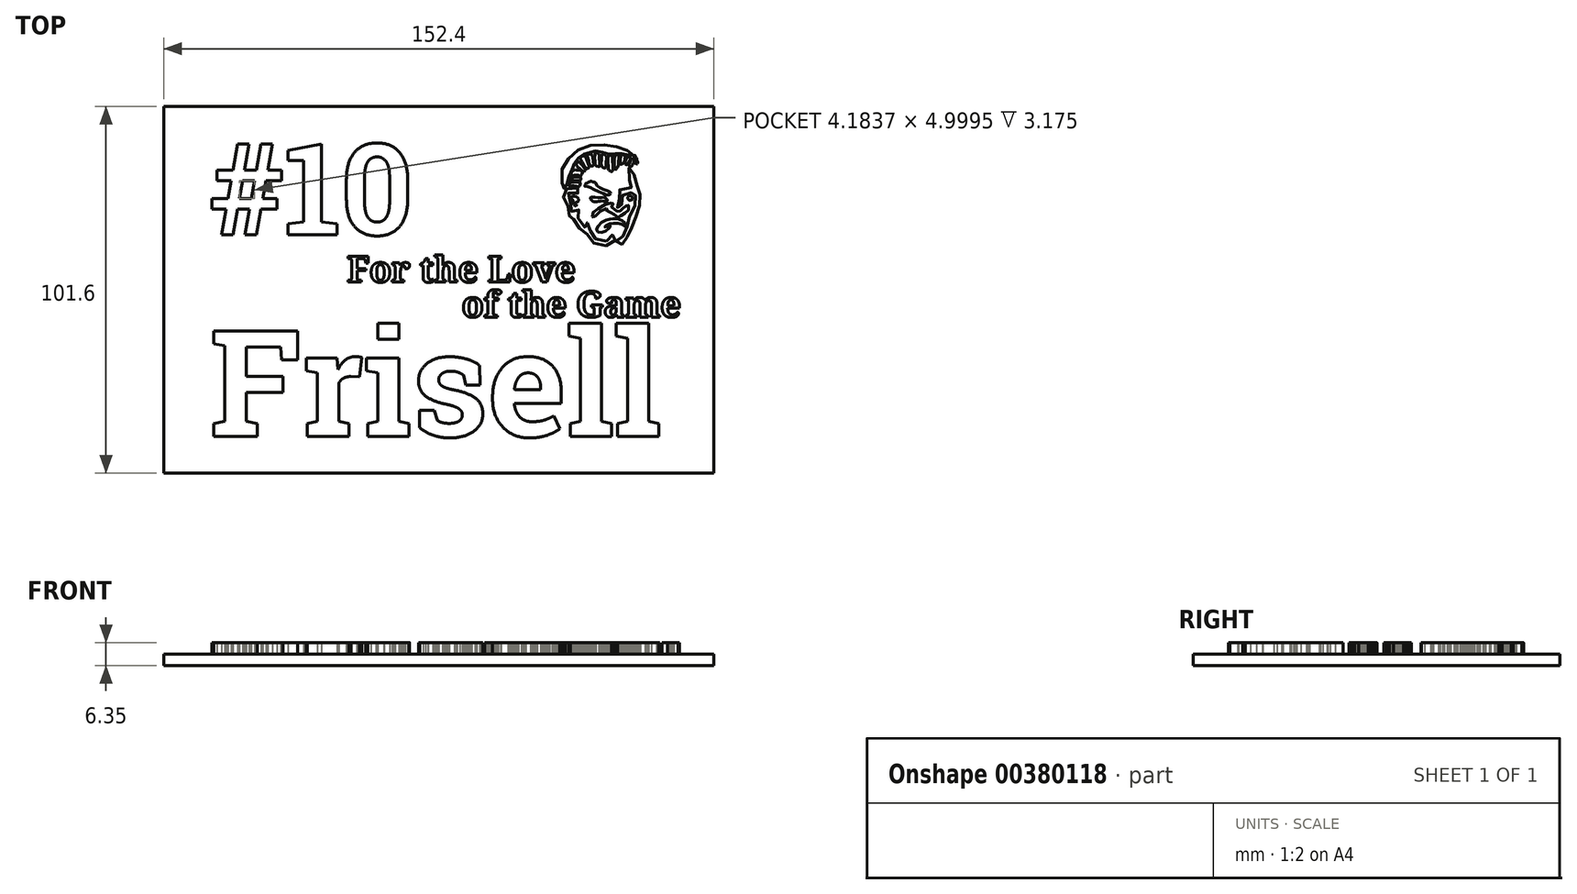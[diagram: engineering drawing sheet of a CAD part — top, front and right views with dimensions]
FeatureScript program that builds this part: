
annotation { "Feature Type Name" : "Feature", "Feature Type Description" : "" }
export const myFeature = defineFeature(function(context is Context, id is Id, definition is map)
    precondition{}
    {
        {
            var Q0;
            Q0=qCreatedBy(makeId("Top.planeOp"),FACE);
            var sketch = newSketch(context, id + "F0", { "sketchPlane" : qUnion([Q0])});
            skLineSegment(sketch, "E0.bottom", {"start": v(-75.13, 26) * mm, "end": v(77.27, 26) * mm});
            skLineSegment(sketch, "E0.top", {"start": v(-75.13, -75.6) * mm, "end": v(77.27, -75.6) * mm});
            skLineSegment(sketch, "E0.left", {"start": v(-75.13, 26) * mm, "end": v(-75.13, -75.6) * mm});
            skLineSegment(sketch, "E0.right", {"start": v(77.27, 26) * mm, "end": v(77.27, -75.6) * mm});
            skSolve(sketch);
        }
        {
            var Q0;
            Q0=makeQuery(id+"F0.imprint","IMPRINT",FACE,{"disambiguationData":[TD([[makeQuery(id+"F0.imprint","IMPRINT",EDGE,{"derivedFrom":sQuery(id+"F0.wireOp",EDGE,"E0.bottom")}),-1.0]])]});
            var sketch = newSketch(context, id + "F1", { "sketchPlane" : qUnion([Q0])});
            skFitSpline(sketch, "E1", {"points": [v(47.57, -11.3) * mm, v(48.35, -11.04) * mm, v(48.7, -10.35) * mm, v(49.04, -9.7) * mm, v(49.57, -9.46) * mm, v(50.02, -9.78) * mm, v(50.06, -10.58) * mm, v(49.74, -11.5) * mm, v(49.1, -12.15) * mm, v(47.63, -12.55) * mm, v(46.12, -12.5) * mm, v(44.61, -12.12) * mm, v(43.38, -11.34) * mm, v(42.6, -10.32) * mm, v(42.24, -9.52) * mm, v(42.15, -9.31) * mm, v(41.34, -8.82) * mm, v(40.33, -8.02) * mm, v(39.44, -7.2) * mm, v(38.67, -6.1) * mm, v(38.42, -5) * mm, v(38.42, -4.22) * mm, v(38.35, -4.2) * mm, v(37.68, -4.39) * mm, v(37.16, -4.27) * mm, v(36.95, -3.72) * mm, v(36.86, -2.5) * mm, v(36.8, -1.48) * mm, v(36.67, -1.07) * mm, v(35.77, 0.2) * mm, v(35.58, 1.07) * mm, v(35.86, 2.13) * mm, v(36.18, 2.7) * mm, v(36.53, 3.12) * mm, v(37.23, 3.22) * mm, v(39.03, 3.4) * mm, v(39.82, 3.34) * mm, v(40.19, 3.09) * mm, v(40.23, 2.45) * mm, v(39.66, 1.98) * mm, v(38.93, 1.9) * mm, v(38.59, 2.03) * mm, v(37.24, 2.03) * mm, v(36.72, 1.65) * mm, v(36.72, 0.85) * mm, v(37.32, -0.2) * mm, v(37.77, -1.18) * mm, v(37.85, -2.09) * mm, v(37.9, -3.1) * mm, v(37.99, -3.1) * mm, v(38.63, -3.1) * mm, v(39.4, -2.76) * mm, v(39.72, -2.59) * mm, v(39.8, -2.7) * mm, v(39.73, -3.22) * mm, v(39.6, -4) * mm, v(39.6, -4.77) * mm, v(40.1, -5.82) * mm, v(41.16, -7.15) * mm, v(41.6, -7.53) * mm, v(41.9, -7.56) * mm, v(41.89, -7.44) * mm, v(41.82, -6.61) * mm, v(42, -6.23) * mm, v(42.5, -6.3) * mm, v(42.8, -6.61) * mm, v(43.05, -7.98) * mm, v(43.22, -8.82) * mm, v(43.51, -9.54) * mm, v(44.12, -10.4) * mm, v(45.11, -11.01) * mm, v(46.32, -11.33) * mm, v(47.57, -11.3) * mm]});
            skFitSpline(sketch, "E2", {"points": [v(47.8, -7.3) * mm, v(47.13, -7.42) * mm, v(47.01, -7.42) * mm, v(47.13, -7.18) * mm, v(48.11, -6.65) * mm, v(49.11, -6.46) * mm, v(50.54, -6.45) * mm, v(51.76, -6.67) * mm, v(52.61, -7.21) * mm, v(52.82, -7.33) * mm, v(52.97, -7.12) * mm, v(52.7, -6.5) * mm, v(52.11, -5.74) * mm, v(50.6, -5.18) * mm, v(49.08, -5.16) * mm, v(48.46, -5.24) * mm, v(47.16, -5.6) * mm, v(45.65, -6.61) * mm, v(44.86, -7.78) * mm, v(44.9, -8.5) * mm, v(45.47, -8.94) * mm, v(46.7, -8.8) * mm, v(47.75, -8.16) * mm, v(48.56, -7.4) * mm, v(48.6, -7.12) * mm, v(47.8, -7.3) * mm]});
            skFitSpline(sketch, "E3", {"points": [v(51.85, -12.22) * mm, v(51.05, -12.44) * mm, v(50.33, -12.28) * mm, v(50.13, -11.73) * mm, v(50.52, -11.04) * mm, v(51.15, -10.86) * mm, v(51.76, -10.57) * mm, v(52.13, -10) * mm, v(52.3, -9.2) * mm, v(52.67, -8.25) * mm, v(53.2, -7.5) * mm, v(53.55, -6.76) * mm, v(53.63, -5.82) * mm, v(53.78, -4.85) * mm, v(54.49, -3.73) * mm, v(55.3, -2.73) * mm, v(55.42, -1.6) * mm, v(55.17, -0.4) * mm, v(55.2, 0.11) * mm, v(55.52, 1.32) * mm, v(55.57, 2.16) * mm, v(55.47, 2.42) * mm, v(54.99, 2.38) * mm, v(54.56, 2.14) * mm, v(53.7, 2.1) * mm, v(52.55, 2.06) * mm, v(52.07, 1.77) * mm, v(51.98, 1.02) * mm, v(52.2, 0.28) * mm, v(52.08, -0.6) * mm, v(51.72, -1.24) * mm, v(51.47, -1.75) * mm, v(51.5, -2.22) * mm, v(51.32, -2.4) * mm, v(50.6, -2.13) * mm, v(50.38, -1.6) * mm, v(50.64, -0.97) * mm, v(51, -0.17) * mm, v(51.06, 0.44) * mm, v(50.78, 1.07) * mm, v(50.66, 1.97) * mm, v(51.18, 2.9) * mm, v(52.12, 3.24) * mm, v(53.3, 3.36) * mm, v(54.52, 3.48) * mm, v(54.66, 3.6) * mm, v(54.38, 3.97) * mm, v(54, 4.8) * mm, v(53.79, 6.28) * mm, v(53.9, 7.94) * mm, v(53.79, 8.9) * mm, v(53.79, 9.1) * mm, v(54.03, 9.04) * mm, v(54.76, 8.52) * mm, v(55.13, 7.38) * mm, v(55.34, 5.97) * mm, v(55.56, 4.72) * mm, v(56.14, 3.87) * mm, v(56.71, 3.56) * mm, v(57.08, 2.91) * mm, v(56.95, 1.93) * mm, v(56.51, 0.55) * mm, v(56.4, -0.31) * mm, v(56.62, -1.36) * mm, v(56.69, -2.19) * mm, v(56.32, -3.56) * mm, v(55.4, -4.86) * mm, v(54.62, -5.8) * mm, v(54.5, -7.08) * mm, v(54.37, -8.24) * mm, v(53.76, -9.26) * mm, v(53.43, -9.82) * mm, v(53.28, -10.59) * mm, v(53.14, -11.27) * mm, v(52.34, -11.95) * mm, v(51.85, -12.22) * mm]});
            skFitSpline(sketch, "E4", {"points": [v(51.65, -4.28) * mm, v(52.13, -3.81) * mm, v(53.02, -3.37) * mm, v(53.66, -2.72) * mm, v(53.77, -1.9) * mm, v(53.38, -1.13) * mm, v(53.21, -1.15) * mm, v(53, -1.68) * mm, v(52.43, -2.14) * mm, v(51.8, -2.46) * mm, v(51.42, -2.92) * mm, v(50.93, -3.27) * mm, v(50.6, -3.17) * mm, v(50.13, -2.68) * mm, v(49.7, -2.46) * mm, v(49.28, -2.45) * mm, v(49, -1.98) * mm, v(49.06, -1.41) * mm, v(49.39, -0.94) * mm, v(49.4, -0.71) * mm, v(48.82, -0.74) * mm, v(47.56, -0.99) * mm, v(45.6, -2.02) * mm, v(44.06, -3.24) * mm, v(43.57, -3.77) * mm, v(43.7, -4.86) * mm, v(43.9, -4.88) * mm, v(44.45, -4.27) * mm, v(46.1, -2.93) * mm, v(47.41, -2.3) * mm, v(47.63, -2.3) * mm, v(47.73, -2.85) * mm, v(48.15, -3.33) * mm, v(48.9, -3.44) * mm, v(49.24, -3.55) * mm, v(49.84, -4.18) * mm, v(50.54, -4.68) * mm, v(51.18, -4.66) * mm, v(51.65, -4.28) * mm]});
            skFitSpline(sketch, "E5", {"points": [v(54.73, 0.39) * mm, v(54.77, 0.82) * mm, v(54.18, 1.2) * mm, v(53.55, 1.02) * mm, v(53.47, 0.3) * mm, v(54.02, 0) * mm, v(54.73, 0.39) * mm]});
            skFitSpline(sketch, "E6", {"points": [v(44.44, -0.47) * mm, v(43.66, -0.25) * mm, v(43.08, 0.44) * mm, v(43.14, 0.75) * mm, v(43.78, 0.8) * mm, v(46.74, 0.78) * mm, v(47.17, 0.7) * mm, v(47.78, -0.13) * mm, v(47.64, -0.32) * mm, v(46.64, -0.26) * mm, v(45.29, -0.32) * mm, v(44.44, -0.47) * mm]});
            skFitSpline(sketch, "E7", {"points": [v(46.65, 1.86) * mm, v(47.46, 1.48) * mm, v(48.33, 1.53) * mm, v(48.69, 2.02) * mm, v(48.54, 2.32) * mm, v(47.26, 2.83) * mm, v(45.32, 3.72) * mm, v(44.79, 4.23) * mm, v(44.53, 4.83) * mm, v(44.13, 5) * mm, v(43.88, 5) * mm, v(43.34, 5.26) * mm, v(43.09, 5.3) * mm, v(42.9, 5.05) * mm, v(42.6, 5.07) * mm, v(42.3, 4.85) * mm, v(42.2, 4.73) * mm, v(41.9, 4.72) * mm, v(41.8, 4.5) * mm, v(41.38, 4.05) * mm, v(41.56, 3.84) * mm, v(42.59, 3.74) * mm, v(43.78, 3.19) * mm, v(46.65, 1.86) * mm]});
            skFitSpline(sketch, "E8", {"points": [v(39.09, -1.2) * mm, v(38.85, -1.02) * mm, v(39.04, -0.63) * mm, v(39.6, -0.4) * mm, v(39.72, 0.33) * mm, v(39.01, 1.06) * mm, v(38.23, 1.1) * mm, v(37.7, 0.65) * mm, v(37.83, 0.29) * mm, v(38.12, 0.15) * mm, v(38.31, -0.34) * mm, v(38.52, -1.23) * mm, v(38.92, -1.63) * mm, v(39.18, -1.51) * mm, v(39.26, -1.2) * mm, v(39.09, -1.2) * mm]});
            skFitSpline(sketch, "E9", {"points": [v(35.18, 4.73) * mm, v(35.4, 3.4) * mm, v(35.76, 3.05) * mm, v(35.87, 3.13) * mm, v(36.08, 3.42) * mm, v(36.43, 3.67) * mm, v(36.66, 4.42) * mm, v(36.6, 5.36) * mm, v(37.02, 6.1) * mm, v(37.15, 6.7) * mm, v(37.23, 7.46) * mm, v(37.88, 8.4) * mm, v(38.45, 9.02) * mm, v(38.56, 9.75) * mm, v(38.74, 10.4) * mm, v(39.17, 10.98) * mm, v(39.64, 11.29) * mm, v(39.78, 11.9) * mm, v(40.12, 12.28) * mm, v(40.85, 12.68) * mm, v(41.65, 12.77) * mm, v(42.03, 12.99) * mm, v(42.91, 13.25) * mm, v(43.49, 13.17) * mm, v(43.91, 13.25) * mm, v(44.22, 13.54) * mm, v(44.87, 13.6) * mm, v(45.62, 13.32) * mm, v(46.3, 13.31) * mm, v(46.91, 13.3) * mm, v(47.51, 12.81) * mm, v(48.11, 12.71) * mm, v(48.8, 12.83) * mm, v(49.39, 12.68) * mm, v(50.13, 12.89) * mm, v(50.83, 12.96) * mm, v(51.35, 12.83) * mm, v(51.87, 12.94) * mm, v(52.53, 12.95) * mm, v(53.18, 12.6) * mm, v(53.93, 12.6) * mm, v(54.48, 12.4) * mm, v(54.65, 12.18) * mm, v(55.03, 12.55) * mm, v(54.73, 12.89) * mm, v(53.9, 13.45) * mm, v(51.53, 14.51) * mm, v(50.44, 14.76) * mm, v(49.1, 15.08) * mm, v(45.83, 15.4) * mm, v(43.17, 15.22) * mm, v(40.97, 14.54) * mm, v(38.6, 13.18) * mm, v(36.98, 11.4) * mm, v(35.34, 9.1) * mm, v(35.2, 8.1) * mm, v(35.18, 4.73) * mm]});
            skFitSpline(sketch, "E10", {"points": [v(39.4, 5) * mm, v(39.96, 4.99) * mm, v(40.23, 4.82) * mm, v(40.1, 4) * mm, v(39.64, 3.78) * mm, v(38.94, 3.9) * mm, v(37.89, 3.94) * mm, v(37.45, 3.8) * mm, v(37.1, 4.04) * mm, v(37.54, 4.84) * mm, v(38.3, 5) * mm, v(39.4, 5) * mm]});
            skFitSpline(sketch, "E11", {"points": [v(37.48, 5.07) * mm, v(37.11, 4.96) * mm, v(36.94, 5.2) * mm, v(37.34, 5.9) * mm, v(37.75, 6.14) * mm, v(39.96, 6.47) * mm, v(40.35, 6.2) * mm, v(40.47, 5.65) * mm, v(40.11, 5.36) * mm, v(39.64, 5.4) * mm, v(38.37, 5.41) * mm, v(37.48, 5.07) * mm]});
            skFitSpline(sketch, "E12", {"points": [v(38.14, 6.82) * mm, v(39.68, 6.88) * mm, v(40, 6.74) * mm, v(40.54, 7) * mm, v(40.85, 7.85) * mm, v(40.67, 8.1) * mm, v(39.1, 8.4) * mm, v(38.41, 8.3) * mm, v(37.9, 7.73) * mm, v(37.48, 6.86) * mm, v(37.68, 6.74) * mm, v(38.14, 6.82) * mm]});
            skFitSpline(sketch, "E13", {"points": [v(39.26, 9.59) * mm, v(41, 8.1) * mm, v(41.32, 7.94) * mm, v(41.68, 8.33) * mm, v(41.53, 8.74) * mm, v(40.44, 10.1) * mm, v(39.87, 10.6) * mm, v(39.5, 10.56) * mm, v(39.13, 10.09) * mm, v(39.26, 9.59) * mm]});
            skFitSpline(sketch, "E14", {"points": [v(40.75, 10.65) * mm, v(40.33, 11.47) * mm, v(40.46, 11.98) * mm, v(41.21, 12.34) * mm, v(41.77, 12.07) * mm, v(42.13, 11.12) * mm, v(42.72, 9.33) * mm, v(42.65, 8.96) * mm, v(42.12, 8.81) * mm, v(41.62, 9.07) * mm, v(40.75, 10.65) * mm]});
            skFitSpline(sketch, "E15", {"points": [v(42.43, 11.4) * mm, v(42.21, 12.24) * mm, v(42.3, 12.64) * mm, v(43, 12.81) * mm, v(43.54, 12.53) * mm, v(43.83, 11.13) * mm, v(44, 9.88) * mm, v(43.65, 9.47) * mm, v(42.94, 9.8) * mm, v(42.43, 11.4) * mm]});
            skFitSpline(sketch, "E16", {"points": [v(44.29, 12.06) * mm, v(44.36, 12.96) * mm, v(44.5, 13.26) * mm, v(44.93, 13.17) * mm, v(45.54, 12.55) * mm, v(45.55, 11.97) * mm, v(45.6, 9.45) * mm, v(45.5, 9.32) * mm, v(44.61, 9.6) * mm, v(44.4, 10.08) * mm, v(44.29, 12.06) * mm]});
            skFitSpline(sketch, "E17", {"points": [v(46.05, 10.51) * mm, v(46.15, 9.53) * mm, v(46.62, 9.04) * mm, v(47.1, 8.88) * mm, v(47.3, 9.08) * mm, v(47.48, 10.9) * mm, v(47.53, 12.07) * mm, v(47.34, 12.46) * mm, v(46.68, 12.84) * mm, v(46.32, 12.79) * mm, v(46.17, 11.97) * mm, v(46.05, 10.51) * mm]});
            skFitSpline(sketch, "E18", {"points": [v(48.03, 8.99) * mm, v(48.11, 8.48) * mm, v(48.48, 8.11) * mm, v(48.94, 7.92) * mm, v(49.21, 8.2) * mm, v(49.24, 10.23) * mm, v(49.16, 12.1) * mm, v(48.83, 12.47) * mm, v(48.44, 12.47) * mm, v(47.98, 12) * mm, v(47.93, 10.87) * mm, v(48.03, 8.99) * mm]});
            skFitSpline(sketch, "E19", {"points": [v(49.71, 9.45) * mm, v(49.86, 8.66) * mm, v(50.13, 8.48) * mm, v(50.3, 8.75) * mm, v(50.76, 9.43) * mm, v(50.85, 10.13) * mm, v(50.93, 12.16) * mm, v(50.81, 12.6) * mm, v(50.31, 12.66) * mm, v(49.83, 12.22) * mm, v(49.7, 11.19) * mm, v(49.71, 9.45) * mm]});
            skFitSpline(sketch, "E20", {"points": [v(51.32, 10.54) * mm, v(51.4, 11.84) * mm, v(51.7, 12.52) * mm, v(52.3, 12.55) * mm, v(52.72, 12.21) * mm, v(52.63, 11.54) * mm, v(52.29, 10.26) * mm, v(51.93, 10.06) * mm, v(51.44, 9.99) * mm, v(51.32, 10.54) * mm]});
            skFitSpline(sketch, "E21", {"points": [v(52.63, 10.38) * mm, v(52.83, 11.01) * mm, v(53.35, 11.9) * mm, v(53.66, 12.08) * mm, v(54.13, 11.71) * mm, v(53.9, 10.95) * mm, v(53.35, 10.1) * mm, v(53.17, 9.86) * mm, v(52.8, 9.99) * mm, v(52.63, 10.38) * mm]});
            skFitSpline(sketch, "E22", {"points": [v(53.86, 10.18) * mm, v(53.7, 9.9) * mm, v(53.81, 9.57) * mm, v(54.15, 9.28) * mm, v(54.42, 9.39) * mm, v(55.14, 10.6) * mm, v(55.26, 11.14) * mm, v(55.02, 11.54) * mm, v(54.8, 11.61) * mm, v(54.48, 11.27) * mm, v(53.86, 10.18) * mm]});
            skFitSpline(sketch, "E23", {"points": [v(55.24, 11.7) * mm, v(55.54, 11.38) * mm, v(55.58, 10.83) * mm, v(55.47, 10.49) * mm, v(55.7, 10.04) * mm, v(55.92, 10.02) * mm, v(56.2, 10.63) * mm, v(56.05, 10.85) * mm, v(55.85, 11.61) * mm, v(55.63, 12) * mm, v(55.42, 12.46) * mm, v(55.15, 12.4) * mm, v(55.09, 11.93) * mm, v(55.24, 11.7) * mm]});
            skText(sketch, "E24", { "text": "For the Love", "fontName": "NotoSerif-Bold.ttf"});
            skText(sketch, "E25", { "text": "of the Game", "fontName": "NotoSerif-Bold.ttf"});
            skText(sketch, "E26", { "text": "#10", "fontName": "RobotoSlab-Bold.ttf"});
            skText(sketch, "E27", { "text": "Frisell", "fontName": "RobotoSlab-Bold.ttf"});
            const initialGuessF1  = {"E24": [-0.02433, -0.0227, 1, 0, 0.00716], "E25": [0.00742, -0.0324, 1, 0, 0.00716], "E26": [-0.06243, -0.00956, 1, 0, 0.0254], "E27": [-0.06243, -0.06544, 1, 0, 0.02958]};
            skSetInitialGuess(sketch, initialGuessF1);
            skSolve(sketch);
        }
        {
            var Q0;
            Q0=qSketchRegion(id+"F0",true);
            extrude(context, id + "F2", {"entities" : qUnion([Q0]), "depth" : 3.17 * mm});
        }
        {
            var Q0;
            Q0=qSketchRegion(id+"F1",true);
            extrude(context, id + "F3", {"entities" : qUnion([Q0]), "operationType" : NewBodyOperationType.ADD, "depth" : 6.35 * mm});
        }
    });
